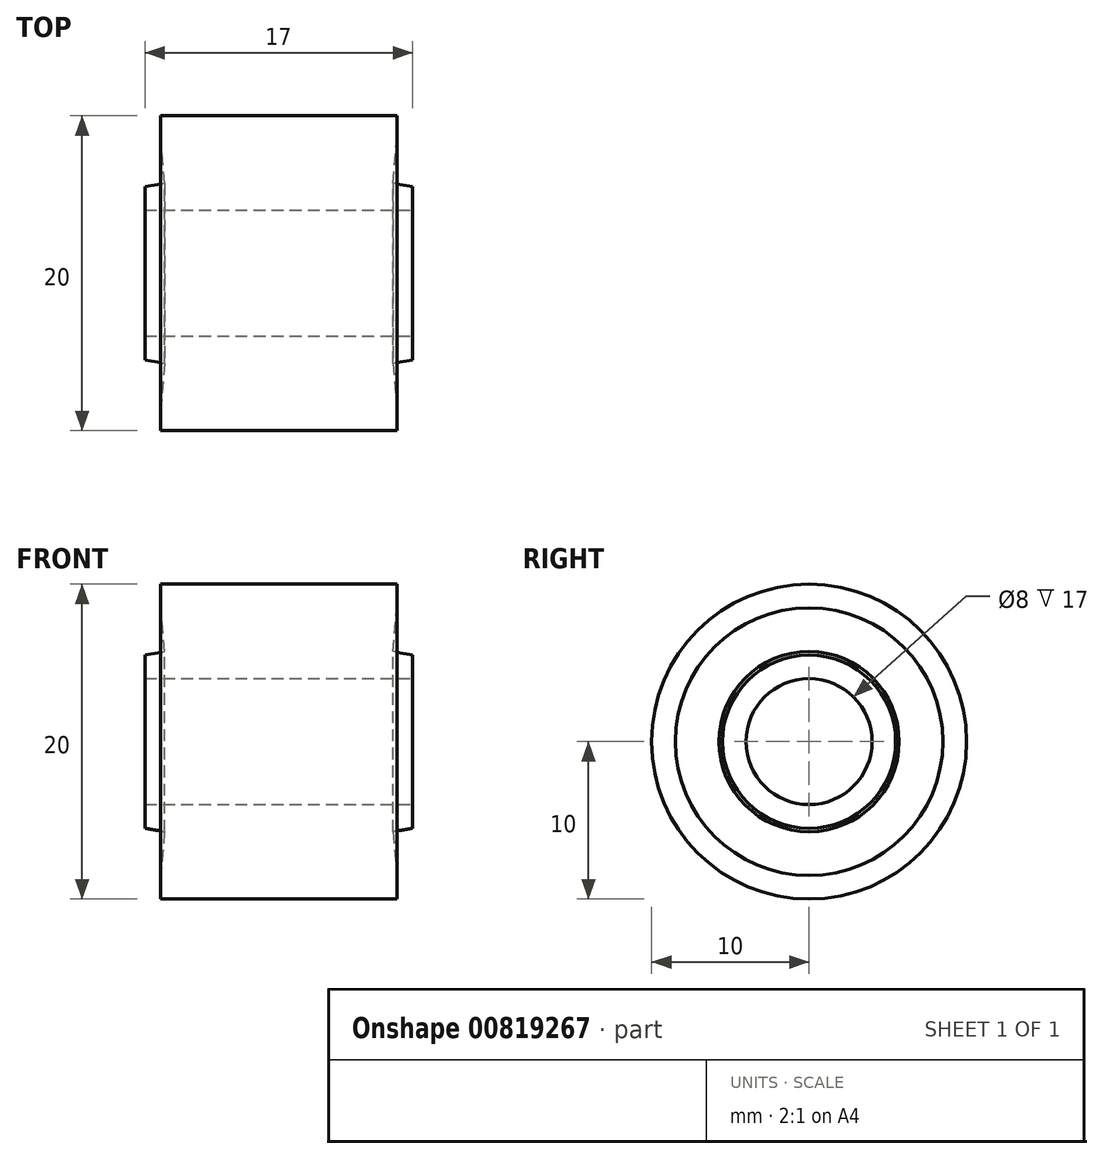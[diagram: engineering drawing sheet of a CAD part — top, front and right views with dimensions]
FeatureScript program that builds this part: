
annotation { "Feature Type Name" : "Feature", "Feature Type Description" : "" }
export const myFeature = defineFeature(function(context is Context, id is Id, definition is map)
    precondition{}
    {
        {
            var Q0;
            Q0=qCreatedBy(makeId("Front.planeOp"),FACE);
            var sketch = newSketch(context, id + "F0", { "sketchPlane" : qUnion([Q0])});
            skLineSegment(sketch, "E0", {"start": v(-7.5, 10) * mm, "end": v(7.5, 10) * mm});
            skLineSegment(sketch, "E1", {"start": v(7.5, 10) * mm, "end": v(7.5, 8.5) * mm});
            skLineSegment(sketch, "E2", {"start": v(8.5, 5.5) * mm, "end": v(8.5, 4) * mm});
            skLineSegment(sketch, "E3", {"start": v(8.5, 4) * mm, "end": v(-8.5, 4) * mm});
            skLineSegment(sketch, "E4", {"start": v(-8.5, 4) * mm, "end": v(-8.5, 5.5) * mm});
            skLineSegment(sketch, "E5", {"start": v(13.1, 0) * mm, "end": v(-17.58, 0) * mm, "construction": true});
            skLineSegment(sketch, "E6", {"start": v(7.5, 8.5) * mm, "end": v(7.26, 5.72) * mm});
            skLineSegment(sketch, "E7", {"start": v(7.26, 5.72) * mm, "end": v(8.5, 5.5) * mm});
            skLineSegment(sketch, "E8", {"start": v(-7.5, 8.5) * mm, "end": v(-7.26, 5.72) * mm});
            skLineSegment(sketch, "E9", {"start": v(-7.26, 5.72) * mm, "end": v(-8.5, 5.5) * mm});
            skLineSegment(sketch, "E10.trimOffspring", {"start": v(-7.5, 8.5) * mm, "end": v(-7.5, 10) * mm});
            skSolve(sketch);
        }
        {
            var Q0;
            Q0=makeQuery(id+"F0.imprint","IMPRINT",FACE,{"disambiguationData":[TD([[makeQuery(id+"F0.imprint","IMPRINT",EDGE,{"derivedFrom":sQuery(id+"F0.wireOp",EDGE,"E0")}),-1.0]])]});
            var Q1;
            Q1=sQuery(id+"F0.wireOp",EDGE,"E5");
            revolve(context, id + "F1", {"surfaceOperationType" : NewSurfaceOperationType.NEW, "entities" : qUnion([Q0]), "axis" : qUnion([Q1]), "revolveType" : RevolveType.FULL});
        }
    });
